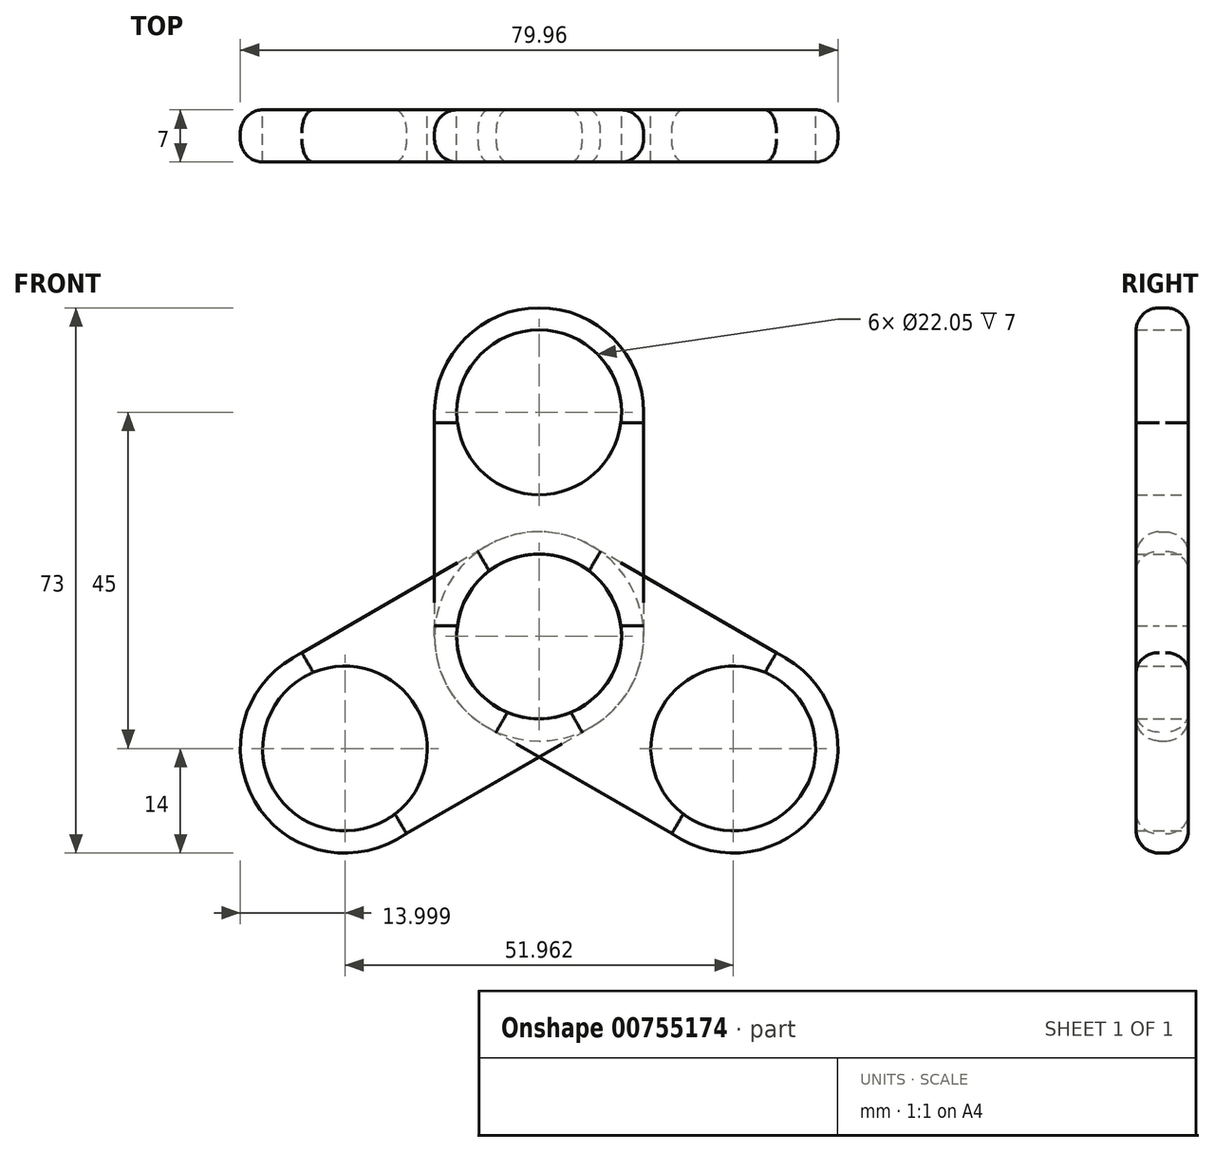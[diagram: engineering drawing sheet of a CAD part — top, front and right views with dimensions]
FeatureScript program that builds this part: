
annotation { "Feature Type Name" : "Feature", "Feature Type Description" : "" }
export const myFeature = defineFeature(function(context is Context, id is Id, definition is map)
    precondition{}
    {
        {
            var Q0;
            Q0=qCreatedBy(makeId("Front.planeOp"),FACE);
            var sketch = newSketch(context, id + "F0", { "sketchPlane" : qUnion([Q0])});
            skLineSegment(sketch, "E0.bottom", {"start": v(14, 15) * mm, "end": v(-14, 15) * mm});
            skLineSegment(sketch, "E0.top", {"start": v(14, -15) * mm, "end": v(-14, -15) * mm});
            skLineSegment(sketch, "E0.left", {"start": v(14, 15) * mm, "end": v(14, -15) * mm});
            skLineSegment(sketch, "E0.right", {"start": v(-14, 15) * mm, "end": v(-14, -15) * mm});
            skPoint(sketch, "E0.middle", {"position": v(0, 0) * mm});
            skCircle(sketch, "E1", {"center": v(0, 15) * mm, "radius": 14 * mm});
            skCircle(sketch, "E2", {"center": v(0, 15) * mm, "radius": 11.03 * mm});
            skCircle(sketch, "E3", {"center": v(0, -15) * mm, "radius": 14 * mm});
            skCircle(sketch, "E4", {"center": v(0, -15) * mm, "radius": 11.03 * mm});
            skSolve(sketch);
        }
        {
            var Q0;
            {var subQ0=sQuery(id+"F0.wireOp",EDGE,"E0.left");Q0=makeQuery(id+"F0.imprint","IMPRINT",FACE,{"disambiguationData":[TD([[makeQuery(id+"F0.imprint","IMPRINT",EDGE,{"derivedFrom":subQ0}),-1.0]])]});}
            var Q1;
            {var subQ1=sQuery(id+"F0.wireOp",EDGE,"E0.bottom");var subQ3=sQuery(id+"F0.wireOp",EDGE,"E2");var subQ4=makeQuery(id+"F0.imprint","INTERSECT",VERTEX,{"disambiguationData":[OD(0.0)],"derivedFrom":[subQ1,subQ3]});Q1=makeQuery(id+"F0.imprint","IMPRINT",FACE,{"disambiguationData":[TD([[makeQuery(id+"F0.imprint","IMPRINT",EDGE,{"disambiguationData":[TD([[subQ4,1.0]])],"derivedFrom":subQ3}),-1.0]])]});}
            var Q2;
            {var subQ1=sQuery(id+"F0.wireOp",EDGE,"E0.bottom");var subQ3=sQuery(id+"F0.wireOp",EDGE,"E2");var subQ4=makeQuery(id+"F0.imprint","INTERSECT",VERTEX,{"disambiguationData":[OD(0.0)],"derivedFrom":[subQ1,subQ3]});Q2=makeQuery(id+"F0.imprint","IMPRINT",FACE,{"disambiguationData":[TD([[makeQuery(id+"F0.imprint","IMPRINT",EDGE,{"disambiguationData":[TD([[subQ4,-1.0]])],"derivedFrom":subQ3}),-1.0]])]});}
            var Q3;
            {var subQ1=sQuery(id+"F0.wireOp",EDGE,"E0.top");var subQ3=sQuery(id+"F0.wireOp",EDGE,"E4");var subQ4=makeQuery(id+"F0.imprint","INTERSECT",VERTEX,{"disambiguationData":[OD(0.0)],"derivedFrom":[subQ1,subQ3]});Q3=makeQuery(id+"F0.imprint","IMPRINT",FACE,{"disambiguationData":[TD([[makeQuery(id+"F0.imprint","IMPRINT",EDGE,{"disambiguationData":[TD([[subQ4,1.0]])],"derivedFrom":subQ3}),-1.0]])]});}
            var Q4;
            {var subQ1=sQuery(id+"F0.wireOp",EDGE,"E0.top");var subQ3=sQuery(id+"F0.wireOp",EDGE,"E4");var subQ4=makeQuery(id+"F0.imprint","INTERSECT",VERTEX,{"disambiguationData":[OD(0.0)],"derivedFrom":[subQ1,subQ3]});Q4=makeQuery(id+"F0.imprint","IMPRINT",FACE,{"disambiguationData":[TD([[makeQuery(id+"F0.imprint","IMPRINT",EDGE,{"disambiguationData":[TD([[subQ4,-1.0]])],"derivedFrom":subQ3}),-1.0]])]});}
            extrude(context, id + "F1", {"entities" : qUnion([Q0, Q1, Q2, Q3, Q4]), "endBound" : BoundingType.SYMMETRIC, "depth" : 7 * mm, "offsetDistance" : 25.4 * mm});
        }
        {
            var Q0;
            Q0=makeQuery(id+"F1.opExtrude","SWEPT_BODY",BODY,{"disambiguationData":[OSD([sQuery(id+"F0.wireOp",EDGE,"E0.left"),sQuery(id+"F0.wireOp",EDGE,"E0.right"),sQuery(id+"F0.wireOp",EDGE,"E1"),sQuery(id+"F0.wireOp",EDGE,"E2"),sQuery(id+"F0.wireOp",EDGE,"E3"),sQuery(id+"F0.wireOp",EDGE,"E4")])]});
            var Q1;
            Q1=makeQuery(id+"F1.opExtrude","SWEPT_FACE",FACE,{"disambiguationData":[OSD([sQuery(id+"F0.wireOp",EDGE,"E3")])]});
            circularPattern(context, id + "F2", {"entities" : qUnion([Q0]), "axis" : qUnion([Q1]), "angle" : 360 * degree, "instanceCount" : 3, "equalSpace" : true});
        }
        {
            var Q0;
            Q0=makeQuery(id+"F2.opPattern","COPY",EDGE,{"derivedFrom":makeQuery(id+"F1.opExtrude","CAP_EDGE",EDGE,{"disambiguationData":[OSD([sQuery(id+"F0.wireOp",EDGE,"E0.left")])],"isStart":true}),"instanceName":"1"});
            var Q1;
            Q1=makeQuery(id+"F2.opPattern","COPY",EDGE,{"derivedFrom":makeQuery(id+"F1.opExtrude","CAP_EDGE",EDGE,{"disambiguationData":[OSD([sQuery(id+"F0.wireOp",EDGE,"E0.right")])],"isStart":true}),"instanceName":"1"});
            var Q2;
            Q2=makeQuery(id+"F2.opPattern","COPY",EDGE,{"derivedFrom":makeQuery(id+"F1.opExtrude","CAP_EDGE",EDGE,{"disambiguationData":[OSD([sQuery(id+"F0.wireOp",EDGE,"E1")])],"isStart":true}),"instanceName":"1"});
            var Q3;
            Q3=makeQuery(id+"F2.opPattern","COPY",EDGE,{"derivedFrom":makeQuery(id+"F1.opExtrude","CAP_EDGE",EDGE,{"disambiguationData":[OSD([sQuery(id+"F0.wireOp",EDGE,"E0.right")])],"isStart":true}),"instanceName":"2"});
            var Q4;
            Q4=makeQuery(id+"F2.opPattern","COPY",EDGE,{"derivedFrom":makeQuery(id+"F1.opExtrude","CAP_EDGE",EDGE,{"disambiguationData":[OSD([sQuery(id+"F0.wireOp",EDGE,"E1")])],"isStart":true}),"instanceName":"2"});
            var Q5;
            Q5=makeQuery(id+"F2.opPattern","COPY",EDGE,{"derivedFrom":makeQuery(id+"F1.opExtrude","CAP_EDGE",EDGE,{"disambiguationData":[OSD([sQuery(id+"F0.wireOp",EDGE,"E0.left")])],"isStart":true}),"instanceName":"2"});
            var Q6;
            Q6=makeQuery(id+"F1.opExtrude","CAP_EDGE",EDGE,{"disambiguationData":[OSD([sQuery(id+"F0.wireOp",EDGE,"E0.right")])],"isStart":true});
            var Q7;
            Q7=makeQuery(id+"F1.opExtrude","CAP_EDGE",EDGE,{"disambiguationData":[OSD([sQuery(id+"F0.wireOp",EDGE,"E1")])],"isStart":true});
            var Q8;
            Q8=makeQuery(id+"F1.opExtrude","CAP_EDGE",EDGE,{"disambiguationData":[OSD([sQuery(id+"F0.wireOp",EDGE,"E0.left")])],"isStart":true});
            var Q9;
            Q9=makeQuery(id+"F1.opExtrude","CAP_EDGE",EDGE,{"disambiguationData":[OSD([sQuery(id+"F0.wireOp",EDGE,"E0.right")])],"isStart":false});
            var Q10;
            Q10=makeQuery(id+"F1.opExtrude","CAP_EDGE",EDGE,{"disambiguationData":[OSD([sQuery(id+"F0.wireOp",EDGE,"E1")])],"isStart":false});
            var Q11;
            Q11=makeQuery(id+"F1.opExtrude","CAP_EDGE",EDGE,{"disambiguationData":[OSD([sQuery(id+"F0.wireOp",EDGE,"E0.left")])],"isStart":false});
            var Q12;
            Q12=makeQuery(id+"F2.opPattern","COPY",EDGE,{"derivedFrom":makeQuery(id+"F1.opExtrude","CAP_EDGE",EDGE,{"disambiguationData":[OSD([sQuery(id+"F0.wireOp",EDGE,"E0.right")])],"isStart":false}),"instanceName":"1"});
            var Q13;
            Q13=makeQuery(id+"F2.opPattern","COPY",EDGE,{"derivedFrom":makeQuery(id+"F1.opExtrude","CAP_EDGE",EDGE,{"disambiguationData":[OSD([sQuery(id+"F0.wireOp",EDGE,"E1")])],"isStart":false}),"instanceName":"1"});
            var Q14;
            Q14=makeQuery(id+"F2.opPattern","COPY",EDGE,{"derivedFrom":makeQuery(id+"F1.opExtrude","CAP_EDGE",EDGE,{"disambiguationData":[OSD([sQuery(id+"F0.wireOp",EDGE,"E0.left")])],"isStart":false}),"instanceName":"1"});
            var Q15;
            Q15=makeQuery(id+"F2.opPattern","COPY",EDGE,{"derivedFrom":makeQuery(id+"F1.opExtrude","CAP_EDGE",EDGE,{"disambiguationData":[OSD([sQuery(id+"F0.wireOp",EDGE,"E0.right")])],"isStart":false}),"instanceName":"2"});
            var Q16;
            Q16=makeQuery(id+"F2.opPattern","COPY",EDGE,{"derivedFrom":makeQuery(id+"F1.opExtrude","CAP_EDGE",EDGE,{"disambiguationData":[OSD([sQuery(id+"F0.wireOp",EDGE,"E1")])],"isStart":false}),"instanceName":"2"});
            var Q17;
            Q17=makeQuery(id+"F2.opPattern","COPY",EDGE,{"derivedFrom":makeQuery(id+"F1.opExtrude","CAP_EDGE",EDGE,{"disambiguationData":[OSD([sQuery(id+"F0.wireOp",EDGE,"E0.left")])],"isStart":false}),"instanceName":"2"});
            fillet(context, id + "F3", {"entities" : qUnion([Q0, Q1, Q2, Q3, Q4, Q5, Q6, Q7, Q8, Q9, Q10, Q11, Q12, Q13, Q14, Q15, Q16, Q17]), "radius" : 3.07 * mm, "tangentPropagation" : true, "allowEdgeOverflow" : false});
        }
    });
